# Revit family: НЕВАТОМ_Фильтр-бокс FV, версия 1
name_source: partatom
category: Арматура воздуховодов
revit_build: Autodesk Revit 2017 (Build: 20170118_1100(x64)
units: mm (PartAtom-declared; Revit-internal decimal feet)

## family parameters
Всегда вертикально = Да
На основе рабочей плоскости = Нет
Общий = Нет
При загрузке вырезать с полостями = Нет
Размер круглого соединителя = Использовать диаметр
Тип детали = Вставляется

## types (9) — shared parameters
ADSK_Единица измерения = шт.
ADSK_Завод-изготовитель = НЕВАТОМ
ADSK_Наименование = Фильтр бокс FV
C = 120 мм
Nevatom_URL = https://t.me
Ключевая пометка = Вентиляция
zero-valued in all types: ADSK_Масса

## per-type parameters (varying)
| type | ADSK_Материал | ADSK_Размер_Высота | ADSK_Размер_Длина | ADSK_Размер_Ширина | B | D | E | H | L | d |
| Фильтр бокс FV-100 | Сталь серая | 202 мм | 200 мм | 210 мм | 200 мм | 100 мм | 210 мм | 202 мм | 100 мм | 106 мм |
| Фильтр бокс FV -125 | Сталь серая | 202 мм | 200 мм | 250 мм | 200 мм | 125 мм | 250 мм | 202 мм | 180 мм | 131 мм |
| Фильтр бокс FV- 160 | Сталь серая | 202 мм | 200 мм | 250 мм | 200 мм | 160 мм | 250 мм | 202 мм | 180 мм | 166 мм |
| Фильтр бокс FV - 200 | Сталь серая | 246 мм | 244 мм | 250 мм | 244 мм | 200 мм | 250 мм | 246 мм | 180 мм | 206 мм |
| Фильтр бокс FV - 250 | Сталь серая | 296 мм | 294 мм | 250 мм | 294 мм | 250 мм | 250 мм | 296 мм | 180 мм | 256 мм |
| Фильтр бокс FV - 315 | Сталь серая | 345 мм | 343 мм | 250 мм | 343 мм | 315 мм | 250 мм | 345 мм | 180 мм | 321 мм |
| Фильтр бокс FV - 355 | Сталь оцинкованная | 395 мм | 393 мм | 250 мм | 393 мм | 355 мм | 250 мм | 395 мм | 140 мм | 361 мм |
| Фильтр бокс FV - 400 | Сталь серая | 450 мм | 448 мм | 250 мм | 448 мм | 400 мм | 250 мм | 450 мм | 140 мм | 406 мм |
| Фильтр бокс FV - 500 | <По категории> | 556 мм | 550 мм | 250 мм | 550 мм | 500 мм | 250 мм | 556 мм | 140 мм | 506 мм |
